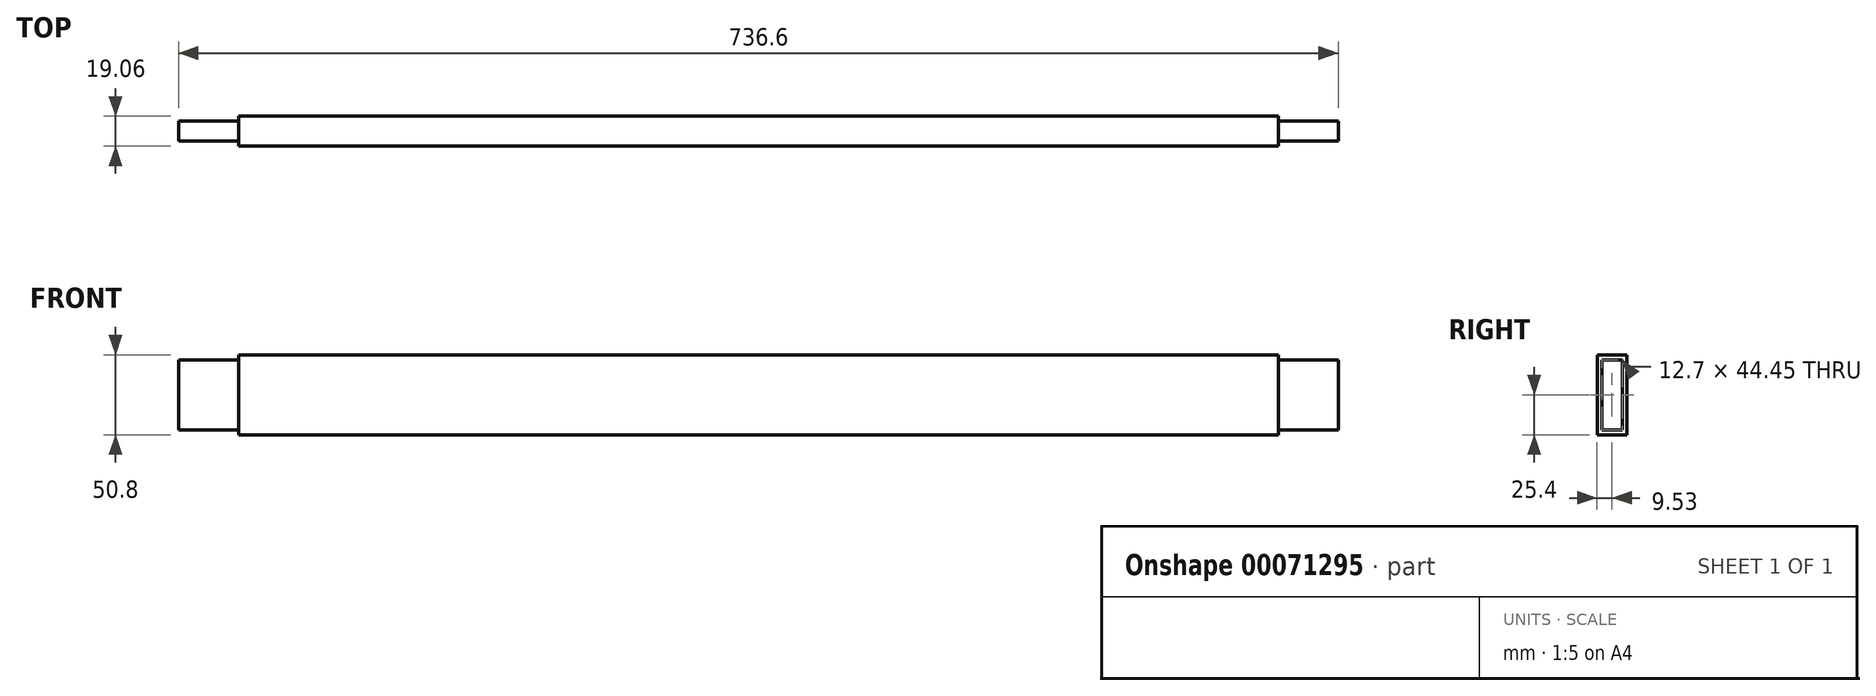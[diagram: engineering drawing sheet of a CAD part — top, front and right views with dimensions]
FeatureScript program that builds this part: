
annotation { "Feature Type Name" : "Feature", "Feature Type Description" : "" }
export const myFeature = defineFeature(function(context is Context, id is Id, definition is map)
    precondition{}
    {
        {
            var Q0;
            Q0=qCreatedBy(makeId("Front.planeOp"),FACE);
            var sketch = newSketch(context, id + "F0", { "sketchPlane" : qUnion([Q0])});
            skLineSegment(sketch, "E0.bottom", {"start": v(-330.2, 25.4) * mm, "end": v(330.2, 25.4) * mm});
            skLineSegment(sketch, "E0.top", {"start": v(-330.2, -25.4) * mm, "end": v(330.2, -25.4) * mm});
            skLineSegment(sketch, "E0.left", {"start": v(-330.2, 25.4) * mm, "end": v(-330.2, -25.4) * mm});
            skLineSegment(sketch, "E0.right", {"start": v(330.2, 25.4) * mm, "end": v(330.2, -25.4) * mm});
            skSolve(sketch);
        }
        {
            var Q0;
            Q0=makeQuery(id+"F0.imprint","IMPRINT",FACE,{"disambiguationData":[TD([[makeQuery(id+"F0.imprint","IMPRINT",EDGE,{"derivedFrom":sQuery(id+"F0.wireOp",EDGE,"E0.bottom")}),-1.0]])]});
            extrude(context, id + "F1", {"entities" : qUnion([Q0]), "endBound" : BoundingType.SYMMETRIC, "depth" : 19.05 * mm});
        }
        {
            var Q0;
            Q0=makeQuery(id+"F1.opExtrude","SWEPT_FACE",FACE,{"disambiguationData":[OSD([sQuery(id+"F0.wireOp",EDGE,"E0.right")])]});
            var sketch = newSketch(context, id + "F2", { "sketchPlane" : qUnion([Q0])});
            skLineSegment(sketch, "E1.bottom", {"start": v(-6.35, 22.22) * mm, "end": v(6.35, 22.22) * mm});
            skLineSegment(sketch, "E1.top", {"start": v(-6.35, -22.23) * mm, "end": v(6.35, -22.23) * mm});
            skLineSegment(sketch, "E1.left", {"start": v(-6.35, 22.22) * mm, "end": v(-6.35, -22.23) * mm});
            skLineSegment(sketch, "E1.right", {"start": v(6.35, 22.22) * mm, "end": v(6.35, -22.23) * mm});
            skSolve(sketch);
        }
        {
            var Q0;
            Q0=makeQuery(id+"F1.opExtrude","SWEPT_FACE",FACE,{"disambiguationData":[OSD([sQuery(id+"F0.wireOp",EDGE,"E0.left")])]});
            var sketch = newSketch(context, id + "F3", { "sketchPlane" : qUnion([Q0])});
            skLineSegment(sketch, "E2.bottom", {"start": v(-6.35, 22.23) * mm, "end": v(6.35, 22.23) * mm});
            skLineSegment(sketch, "E2.top", {"start": v(-6.35, -22.23) * mm, "end": v(6.35, -22.23) * mm});
            skLineSegment(sketch, "E2.left", {"start": v(-6.35, 22.23) * mm, "end": v(-6.35, -22.23) * mm});
            skLineSegment(sketch, "E2.right", {"start": v(6.35, 22.23) * mm, "end": v(6.35, -22.23) * mm});
            skSolve(sketch);
        }
        {
            var Q0;
            Q0 = qSketchRegion(id + "F2", true);
            var Q1;
            Q1=makeQuery(id+"F3.imprint","IMPRINT",FACE,{"disambiguationData":[TD([[makeQuery(id+"F3.imprint","IMPRINT",EDGE,{"derivedFrom":sQuery(id+"F3.wireOp",EDGE,"E2.bottom")}),-1.0]])]});
            extrude(context, id + "F4", {"entities" : qUnion([Q0, Q1]), "operationType" : NewBodyOperationType.ADD, "depth" : 38.1 * mm});
        }
        {
            var Q0;
            Q0=makeQuery(id+"F3.imprint","IMPRINT",FACE,{"disambiguationData":[TD([[makeQuery(id+"F3.imprint","IMPRINT",EDGE,{"derivedFrom":sQuery(id+"F3.wireOp",EDGE,"E2.bottom")}),-1.0]])]});
            extrude(context, id + "F5", {"entities" : qUnion([Q0]), "operationType" : NewBodyOperationType.ADD, "depth" : 38.1 * mm});
        }
    });
